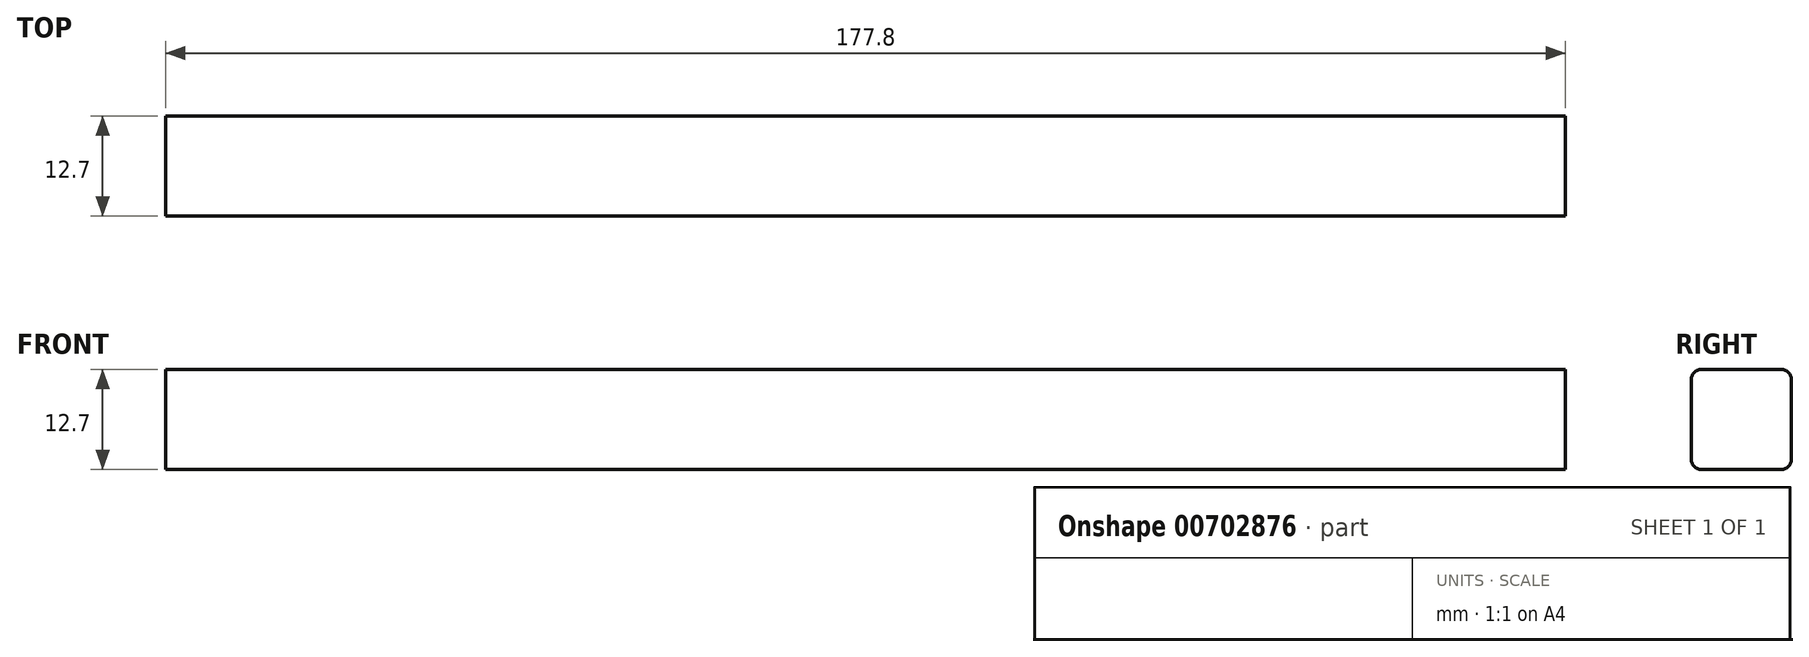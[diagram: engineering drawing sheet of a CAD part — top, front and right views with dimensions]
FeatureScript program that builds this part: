
annotation { "Feature Type Name" : "Feature", "Feature Type Description" : "" }
export const myFeature = defineFeature(function(context is Context, id is Id, definition is map)
    precondition{}
    {
        {
            var Q0;
            Q0=qCreatedBy(makeId("Top.planeOp"),FACE);
            var sketch = newSketch(context, id + "F0", { "sketchPlane" : qUnion([Q0])});
            skLineSegment(sketch, "E0.bottom", {"start": v(88.9, -6.35) * mm, "end": v(-88.9, -6.35) * mm});
            skLineSegment(sketch, "E0.top", {"start": v(88.9, 6.35) * mm, "end": v(-88.9, 6.35) * mm});
            skLineSegment(sketch, "E0.left", {"start": v(88.9, -6.35) * mm, "end": v(88.9, 6.35) * mm});
            skLineSegment(sketch, "E0.right", {"start": v(-88.9, -6.35) * mm, "end": v(-88.9, 6.35) * mm});
            skPoint(sketch, "E0.middle", {"position": v(0, 0) * mm});
            skSolve(sketch);
        }
        {
            var Q0;
            Q0=makeQuery(id+"F0.imprint","IMPRINT",FACE,{"disambiguationData":[TD([[makeQuery(id+"F0.imprint","IMPRINT",EDGE,{"derivedFrom":sQuery(id+"F0.wireOp",EDGE,"E0.bottom")}),-1.0]])]});
            extrude(context, id + "F1", {"entities" : qUnion([Q0]), "depth" : 12.7 * mm, "offsetDistance" : 25.4 * mm});
        }
        {
            var Q0;
            Q0=makeQuery(id+"F1.opExtrude","CAP_EDGE",EDGE,{"disambiguationData":[OSD([sQuery(id+"F0.wireOp",EDGE,"E0.top")])],"isStart":false});
            var Q1;
            Q1=makeQuery(id+"F1.opExtrude","CAP_EDGE",EDGE,{"disambiguationData":[OSD([sQuery(id+"F0.wireOp",EDGE,"E0.bottom")])],"isStart":false});
            var Q2;
            Q2=makeQuery(id+"F1.opExtrude","CAP_EDGE",EDGE,{"disambiguationData":[OSD([sQuery(id+"F0.wireOp",EDGE,"E0.top")])],"isStart":true});
            var Q3;
            Q3=makeQuery(id+"F1.opExtrude","CAP_EDGE",EDGE,{"disambiguationData":[OSD([sQuery(id+"F0.wireOp",EDGE,"E0.bottom")])],"isStart":true});
            fillet(context, id + "F2", {"entities" : qUnion([Q0, Q1, Q2, Q3]), "radius" : 1.27 * mm, "tangentPropagation" : true, "allowEdgeOverflow" : false});
        }
    });
